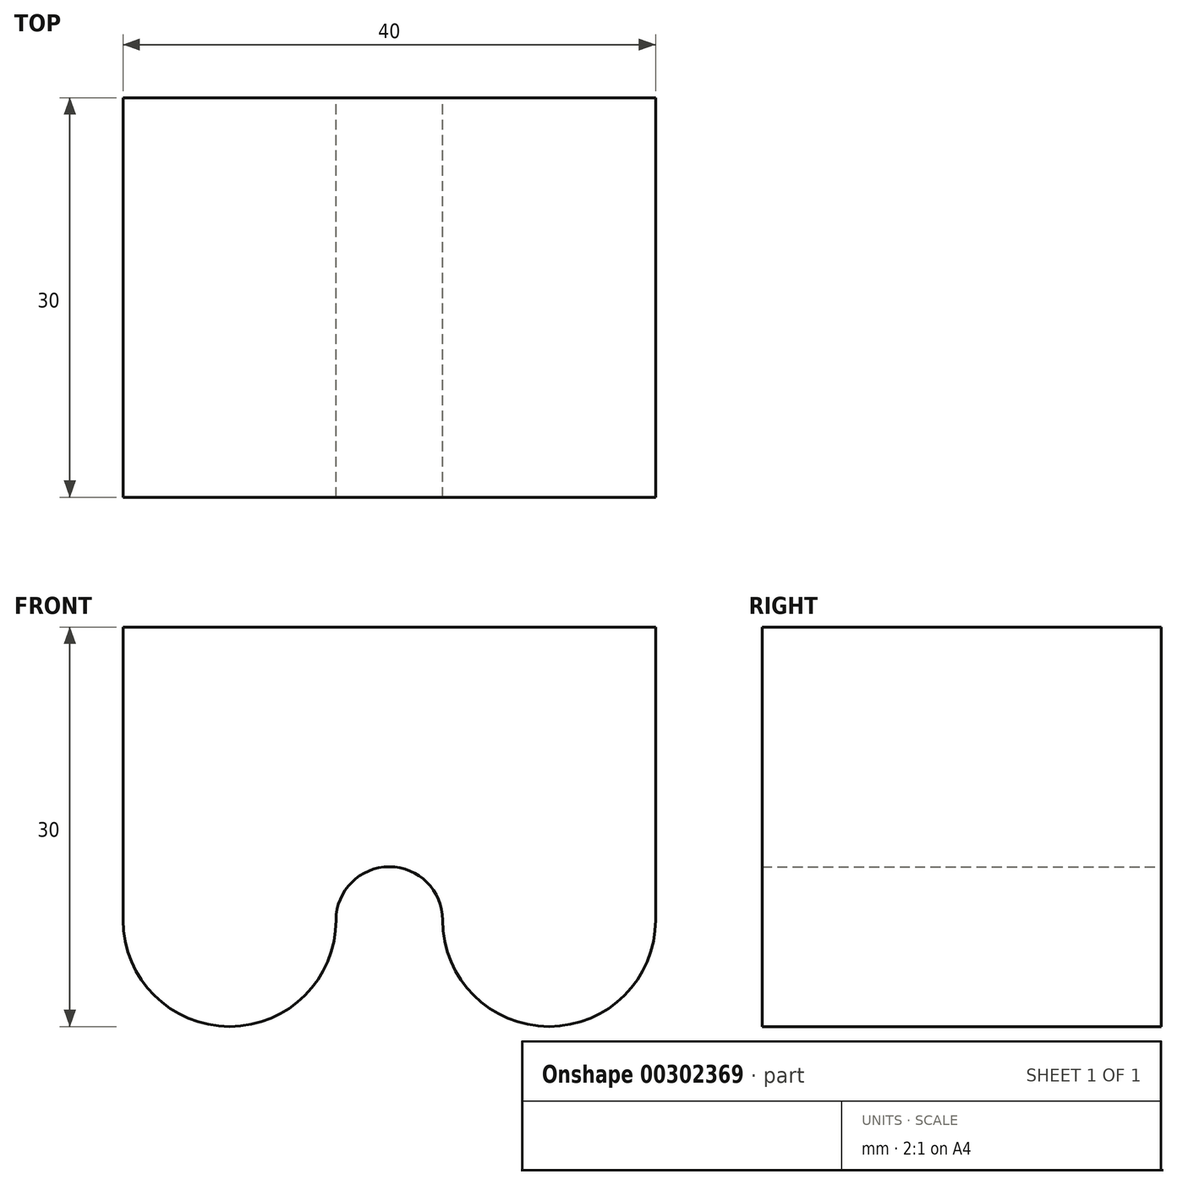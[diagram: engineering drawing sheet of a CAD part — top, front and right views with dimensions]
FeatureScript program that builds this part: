
annotation { "Feature Type Name" : "Feature", "Feature Type Description" : "" }
export const myFeature = defineFeature(function(context is Context, id is Id, definition is map)
    precondition{}
    {
        {
            var Q0;
            Q0=qCreatedBy(makeId("Front.planeOp"),FACE);
            var sketch = newSketch(context, id + "F0", { "sketchPlane" : qUnion([Q0])});
            skLineSegment(sketch, "E0.bottom", {"start": v(-20, -15) * mm, "end": v(20, -15) * mm});
            skLineSegment(sketch, "E0.top", {"start": v(-20, 15) * mm, "end": v(20, 15) * mm});
            skLineSegment(sketch, "E0.left", {"start": v(-20, -15) * mm, "end": v(-20, 15) * mm});
            skLineSegment(sketch, "E0.right", {"start": v(20, -15) * mm, "end": v(20, 15) * mm});
            skPoint(sketch, "E0.middle", {"position": v(0, 0) * mm});
            skArc(sketch, "E1", {"start": v(-20, -7) * mm, "mid": v(-12, -15) * mm, "end": v(-4, -7) * mm});
            skArc(sketch, "E2", {"start": v(4, -7) * mm, "mid": v(12, -15) * mm, "end": v(20, -7) * mm});
            skPoint(sketch, "E3.centerSnap0", {"position": v(0, -15) * mm});
            skArc(sketch, "E4", {"start": v(4, -7) * mm, "mid": v(0, -3) * mm, "end": v(-4, -7) * mm});
            skSolve(sketch);
        }
        {
            var Q0;
            {var subQ1=sQuery(id+"F0.wireOp",EDGE,"E0.top");Q0=makeQuery(id+"F0.imprint","IMPRINT",FACE,{"disambiguationData":[TD([[makeQuery(id+"F0.imprint","IMPRINT",EDGE,{"derivedFrom":subQ1}),-1.0]])]});}
            extrude(context, id + "F1", {"entities" : qUnion([Q0]), "offsetDistance" : 25 * mm, "depth" : 30 * mm});
        }
    });
